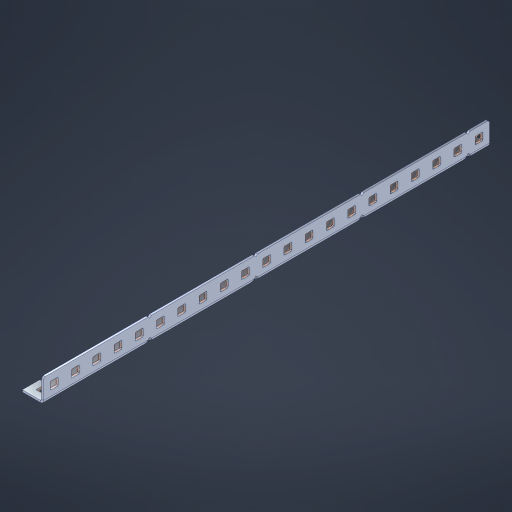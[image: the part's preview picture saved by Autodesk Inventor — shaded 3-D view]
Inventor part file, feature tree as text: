
AUTODESK INVENTOR PART (.ipt)
format: ipt  version: 2023 (Build 270158000, 158)  size: 980,480 bytes
history: native  units: in
note: dims shown in document units (in); Inventor stores cm internally (conversion verified against a paired STEP export)
features: other x70, extrude x61, sheet_metal_op x11, sketch x10, pattern_linear x2, mirror x1, chamfer x1
ambient origin geometry x8: Origin, YZ Plane, XZ Plane, XY Plane, X Axis, Y Axis, Z Axis, Center Point
bodies: Solid1 (feature_tree), Body (feature_tree)
feature tree (156):
  sheet_metal_op  "Flanges"
  other  "Flange Pattern Plane"
  other  "Flange Pattern Sketch"
  sheet_metal_op  "Flange Pattern"
  sheet_metal_op  "Body Pattern"
  pattern_linear  "Center Pattern"  Spacing1=0.0469in  [1 undecoded]
  other  "Arc Length"
  mirror  "Notch Mirror"
  pattern_linear  "Notch Pattern"  Spacing1=0.182in  [1 undecoded]
  chamfer  "End Chamfer"
  extrude  "Half Cut"  Depth=0.02in
  sketch  "Sketch1"  dims[d0=1.0in]
  other  "Plate1"
  sketch  "Sketch2"  dims[d1=10.5in]
  other  "Plate2"
  sheet_metal_op  "Bend1"
  sheet_metal_op  "Corner1"
  sketch  "Sketch3"  dims[d2=0.0469in]
  sketch  "Sketch7"  dims[d3=0.0469in]
  other  "Srf1"
  other  "Srf2"
  sketch  "Sketch8"  dims[d4=0.0234in]
  sketch  "Sketch9"  dims[d5=0.0938in]
  other  "Srf91"
  sheet_metal_op  "Body Pattern Sketch"
  other  "Srf92"
  sketch  "Sketch13"  dims[d6=0.0469in]
  sketch  "Sketch14"  dims[d7=0.5in d8=90.0deg d9=0.0312in]
  sketch  "Sketch15"  dims[d10=0.1875in]
  sketch  "Sketch16"  dims[d11=0.0469in d12=0.0469in d16=0.182in d17=0.02in d18=0.0469in d19=0.0in d20=0.25in d21=0.25in d38=8.2677in d40=0.5in d41=0.3937in d43=1.0in d46=0.172in d47=1.0in d48=0.0in d49=0.182in d50=0.02in d51=0.25in d52=0.25in d53=0.0469in d54=0.0in d55=0.172in d56=1.0in d57=0.0in d58=0.25in d60=8.2677in d62=0.5in d63=0.3937in d65=0.5in d85=0.1227in d86=0.1659in d88=0.04in d89=0.0469in d90=0.0in d91=0.04in d92=0.0491in d95=2.5in d96=0.04in d97=0.25in d98=45.0deg d99=0.25in d100=0.5in d101=0.0in d102=2.497in d106=0.182in d107=0.02in d108=0.5in d109=0.5in d110=0.0469in d111=0.0in d112=0.172in d113=0.5in d114=0.0in d117=0.5in d118=0.5in d119=0.5in]
  other  "Srf786"
  other  "Srf823"
  other  "Srf824"
  other  "Srf825"
  other  "Srf826"
  other  "Srf827"
  other  "Srf828"
  other  "Srf829"
  other  "Srf856"
  other  "Srf857"
  other  "Srf858"
  other  "Srf859"
  other  "Srf860"
  other  "Srf861"
  other  "Srf862"
  other  "Srf889"
  other  "Srf890"
  other  "Srf891"
  other  "Srf892"
  other  "Srf893"
  other  "Srf894"
  other  "Srf895"
  other  "Srf896"
  other  "Srf922"
  other  "Srf923"
  other  "Srf924"
  other  "Srf925"
  other  "Srf926"
  other  "Srf959"
  other  "Srf960"
  other  "Srf961"
  other  "Srf962"
  other  "Srf963"
  other  "Srf996"
  other  "Srf997"
  other  "Srf998"
  other  "Srf999"
  other  "Srf1000"
  other  "Srf1143"
  other  "Srf1144"
  other  "Srf1145"
  other  "Srf1146"
  other  "Srf1147"
  other  "Srf1148"
  other  "Srf1149"
  other  "Srf1199"
  other  "Srf1200"
  other  "Srf1201"
  other  "Srf1202"
  other  "Srf1203"
  other  "Srf1204"
  other  "Srf1205"
  other  "Srf1255"
  other  "Srf1256"
  other  "Srf1257"
  other  "Srf1258"
  other  "Srf1259"
  other  "Srf1260"
  other  "Srf1261"
  sheet_metal_op  "Flange Stamp"
  sheet_metal_op  "Flange Circle"
  sheet_metal_op  "Body Stamp"
  sheet_metal_op  "Body Circle"
  other  "Center Stamp"
  other  "Center Circle"
  sheet_metal_op  "Notch"
  extrude  "ExtrusionSrf2"  Depth=0.0469in
  extrude  "ExtrusionSrf92"  TaperAngle=0.0deg  [1 undecoded]
  extrude  "ExtrusionSrf823"  Depth=0.5in
  extrude  "ExtrusionSrf824"  Depth=0.5in
  extrude  "ExtrusionSrf825"  Depth=0.5in
  extrude  "ExtrusionSrf826"  Depth=0.5in
  extrude  "ExtrusionSrf827"  Depth=1.0in TaperAngle=0.0deg
  extrude  "ExtrusionSrf828"  Depth=0.182in
  extrude  "ExtrusionSrf829"  Depth=0.02in
  extrude  "ExtrusionSrf856"  Depth=0.5in
  extrude  "ExtrusionSrf857"  Depth=0.5in
  extrude  "ExtrusionSrf858"  Depth=0.0469in
  extrude  "ExtrusionSrf859"  TaperAngle=0.0deg  [1 undecoded]
  extrude  "ExtrusionSrf860"  Depth=0.5in
  extrude  "ExtrusionSrf861"  Depth=1.0in TaperAngle=0.0deg
  extrude  "ExtrusionSrf862"  Depth=0.5in
  extrude  "ExtrusionSrf889"  Depth=0.5in
  extrude  "ExtrusionSrf890"  Depth=0.5in
  extrude  "ExtrusionSrf891"  Depth=0.5in
  extrude  "ExtrusionSrf892"  Depth=0.5in
  extrude  "ExtrusionSrf893"  Depth=0.5in
  extrude  "ExtrusionSrf894"  Depth=0.0469in
  extrude  "ExtrusionSrf895"  TaperAngle=0.0deg  [1 undecoded]
  extrude  "ExtrusionSrf896"  Depth=0.5in
  extrude  "ExtrusionSrf922"  Depth=0.5in
  extrude  "ExtrusionSrf923"  Depth=0.5in
  extrude  "ExtrusionSrf924"  Depth=0.5in TaperAngle=45.0deg
  extrude  "ExtrusionSrf925"  Depth=0.5in
  extrude  "ExtrusionSrf926"  Depth=0.5in TaperAngle=0.0deg
  extrude  "ExtrusionSrf959"  Depth=0.5in
  extrude  "ExtrusionSrf960"  Depth=0.182in
  extrude  "ExtrusionSrf961"  Depth=0.02in
  extrude  "ExtrusionSrf962"  Depth=0.5in
  extrude  "ExtrusionSrf963"  Depth=0.5in
  extrude  "ExtrusionSrf996"  Depth=0.0469in
  extrude  "ExtrusionSrf997"  TaperAngle=0.0deg  [1 undecoded]
  extrude  "ExtrusionSrf998"  Depth=0.5in
  extrude  "ExtrusionSrf999"  Depth=0.5in TaperAngle=0.0deg
  extrude  "ExtrusionSrf1000"  Depth=0.5in
  extrude  "ExtrusionSrf1143"  Depth=0.5in
  extrude  "ExtrusionSrf1144"  Depth=0.5in
  extrude  "ExtrusionSrf1145"  [1 undecoded]
  extrude  "ExtrusionSrf1146"  [1 undecoded]
  extrude  "ExtrusionSrf1147"  [1 undecoded]
  extrude  "ExtrusionSrf1148"  [1 undecoded]
  extrude  "ExtrusionSrf1149"  [1 undecoded]
  extrude  "ExtrusionSrf1199"  [1 undecoded]
  extrude  "ExtrusionSrf1200"  [1 undecoded]
  extrude  "ExtrusionSrf1201"  [1 undecoded]
  extrude  "ExtrusionSrf1202"  [1 undecoded]
  extrude  "ExtrusionSrf1203"  [1 undecoded]
  extrude  "ExtrusionSrf1204"  [1 undecoded]
  extrude  "ExtrusionSrf1205"  [1 undecoded]
  extrude  "ExtrusionSrf1255"  [1 undecoded]
  extrude  "ExtrusionSrf1256"  [1 undecoded]
  extrude  "ExtrusionSrf1257"  [1 undecoded]
  extrude  "ExtrusionSrf1258"  [1 undecoded]
  extrude  "ExtrusionSrf1259"  [1 undecoded]
  extrude  "ExtrusionSrf1260"  [1 undecoded]
  extrude  "ExtrusionSrf1261"  [1 undecoded]
note: 25 required parameter values undecoded (feature->parameter linkage not recoverable at this tier; creation-order binding heuristic only, values carry confidence <= 0.55)
